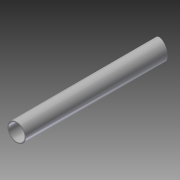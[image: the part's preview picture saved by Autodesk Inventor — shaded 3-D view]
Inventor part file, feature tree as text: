
AUTODESK INVENTOR PART (.ipt)
format: ipt  version: 2013 (Build 170138000, 138)  size: 84,480 bytes
history: native  units: in
note: dims shown in document units (in); Inventor stores cm internally (conversion verified against a paired STEP export)
features: sketch x3, extrude x2, plane x1
ambient origin geometry x8: Origin, YZ Plane, XZ Plane, XY Plane, X Axis, Y Axis, Z Axis, Center Point
bodies: Solid1 (feature_tree)
feature tree (6):
  extrude  "Extrusion1"  Depth=1.33in
  plane  "Work Plane1"
  extrude  "Extrusion2"  TaperAngle=15.0deg  [1 undecoded]
  sketch  "Sketch3"  dims[d6=2.0in d7=0.0in]
  sketch  "Sketch1"  dims[d0=1.5in d2=1.33in]
  sketch  "Sketch2"  dims[d3=12.0in d4=0.0in d5=15.0deg]
note: 1 required parameter value undecoded (feature->parameter linkage not recoverable at this tier; creation-order binding heuristic only, values carry confidence <= 0.55)
